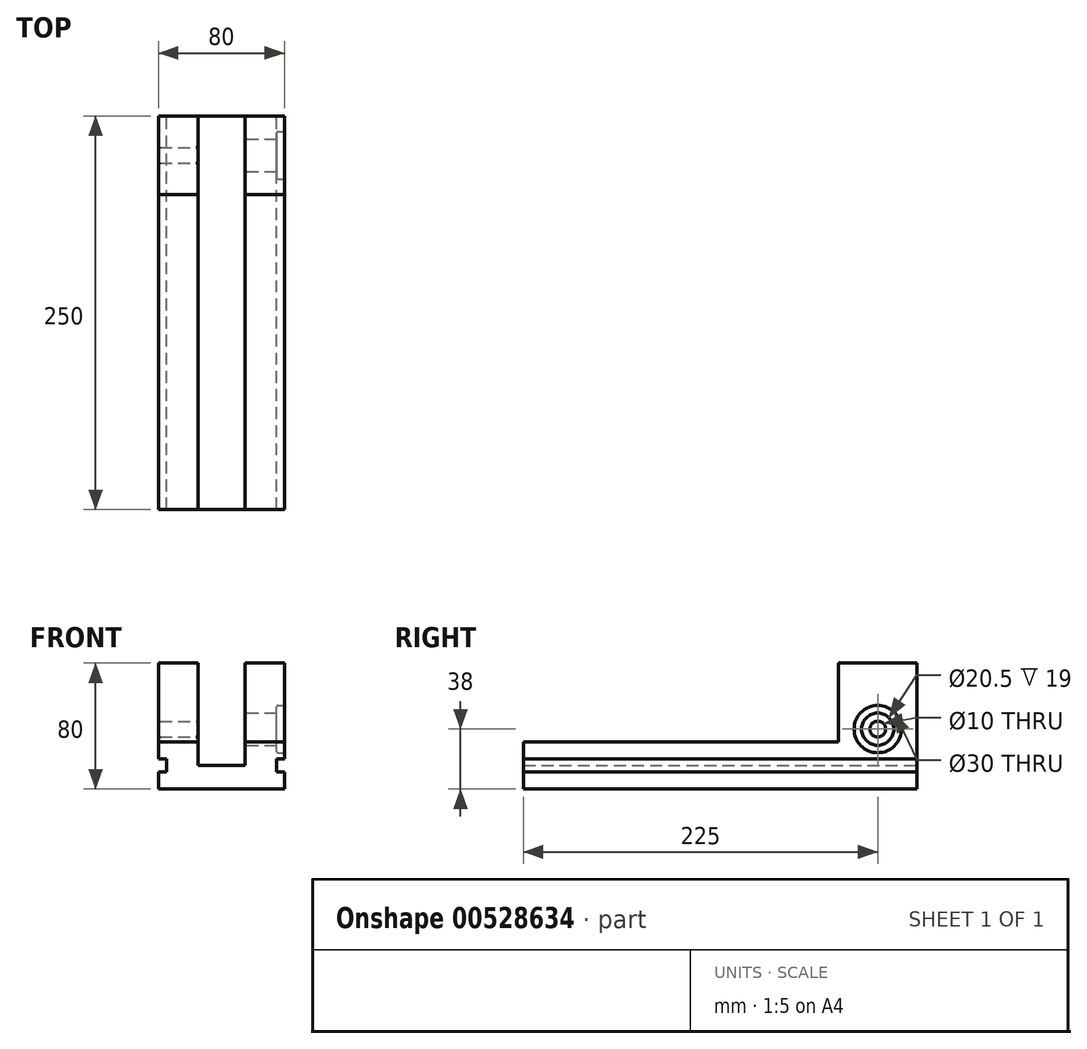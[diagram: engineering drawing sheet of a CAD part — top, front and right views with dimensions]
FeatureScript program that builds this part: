
annotation { "Feature Type Name" : "Feature", "Feature Type Description" : "" }
export const myFeature = defineFeature(function(context is Context, id is Id, definition is map)
    precondition{}
    {
        {
            var Q0;
            Q0=qCreatedBy(makeId("Front.planeOp"),FACE);
            var sketch = newSketch(context, id + "F0", { "sketchPlane" : qUnion([Q0])});
            skLineSegment(sketch, "E0.bottom", {"start": v(40, -15) * mm, "end": v(-40, -15) * mm});
            skLineSegment(sketch, "E0.top", {"start": v(40, 15) * mm, "end": v(15, 15) * mm});
            skLineSegment(sketch, "E0.left", {"start": v(40, -15) * mm, "end": v(40, -4) * mm});
            skLineSegment(sketch, "E0.right", {"start": v(-40, -15) * mm, "end": v(-40, -4) * mm});
            skPoint(sketch, "E0.middle", {"position": v(0, 0) * mm});
            skLineSegment(sketch, "E1", {"start": v(-15, 0) * mm, "end": v(15, 0) * mm});
            skLineSegment(sketch, "E2", {"start": v(-15, 0) * mm, "end": v(-15, 15) * mm});
            skLineSegment(sketch, "E3", {"start": v(15, 0) * mm, "end": v(15, 15) * mm});
            skLineSegment(sketch, "E4.trimOffspring", {"start": v(-15, 15) * mm, "end": v(-40, 15) * mm});
            skLineSegment(sketch, "E5", {"start": v(-40, 4) * mm, "end": v(-35, 4) * mm});
            skLineSegment(sketch, "E6", {"start": v(-35, 4) * mm, "end": v(-35, -4) * mm});
            skLineSegment(sketch, "E7", {"start": v(-35, -4) * mm, "end": v(-40, -4) * mm});
            skLineSegment(sketch, "E8.MirrorCS", {"start": v(35, 4) * mm, "end": v(35, -4) * mm});
            skLineSegment(sketch, "E9.MirrorCS", {"start": v(40, 4) * mm, "end": v(35, 4) * mm});
            skLineSegment(sketch, "E10.MirrorCS", {"start": v(35, -4) * mm, "end": v(40, -4) * mm});
            skLineSegment(sketch, "E11.trimOffspring", {"start": v(-40, 4) * mm, "end": v(-40, 15) * mm});
            skLineSegment(sketch, "E12.trimOffspring", {"start": v(40, 4) * mm, "end": v(40, 15) * mm});
            skSolve(sketch);
        }
        {
            var Q0;
            Q0=makeQuery(id+"F0.imprint","IMPRINT",FACE,{"disambiguationData":[TD([[makeQuery(id+"F0.imprint","IMPRINT",EDGE,{"derivedFrom":sQuery(id+"F0.wireOp",EDGE,"E0.bottom")}),-1.0]])]});
            extrude(context, id + "F1", {"entities" : qUnion([Q0]), "depth" : 250 * mm, "offsetDistance" : 25 * mm});
        }
        {
            var Q0;
            Q0=makeQuery(id+"F1.opExtrude","SWEPT_FACE",FACE,{"disambiguationData":[OSD([sQuery(id+"F0.wireOp",EDGE,"E4.trimOffspring")])]});
            var sketch = newSketch(context, id + "F2", { "sketchPlane" : qUnion([Q0])});
            skLineSegment(sketch, "E13.0.0", {"start": v(-15, 0) * mm, "end": v(-40, 0) * mm});
            skLineSegment(sketch, "E13.0.1", {"start": v(-40, 0) * mm, "end": v(-40, -250) * mm});
            skLineSegment(sketch, "E13.0.2", {"start": v(-40, -250) * mm, "end": v(-15, -250) * mm});
            skLineSegment(sketch, "E13.0.3", {"start": v(-15, -250) * mm, "end": v(-15, 0) * mm});
            skLineSegment(sketch, "E14.0.0", {"start": v(40, 0) * mm, "end": v(15, 0) * mm});
            skLineSegment(sketch, "E14.0.1", {"start": v(15, 0) * mm, "end": v(15, -250) * mm});
            skLineSegment(sketch, "E14.0.2", {"start": v(15, -250) * mm, "end": v(40, -250) * mm});
            skLineSegment(sketch, "E14.0.3", {"start": v(40, -250) * mm, "end": v(40, 0) * mm});
            skLineSegment(sketch, "E15", {"start": v(-40, -50) * mm, "end": v(-15, -50) * mm});
            skLineSegment(sketch, "E16.MirrorCS", {"start": v(40, -50) * mm, "end": v(15, -50) * mm});
            skSolve(sketch);
        }
        {
            var Q0;
            {var subQ0=sQuery(id+"F2.wireOp",EDGE,"E13.0.0");Q0=makeQuery(id+"F2.imprint","IMPRINT",FACE,{"disambiguationData":[TD([[makeQuery(id+"F2.imprint","IMPRINT",EDGE,{"derivedFrom":subQ0}),1.0]])]});}
            var Q1;
            {var subQ0=sQuery(id+"F2.wireOp",EDGE,"E14.0.0");Q1=makeQuery(id+"F2.imprint","IMPRINT",FACE,{"disambiguationData":[TD([[makeQuery(id+"F2.imprint","IMPRINT",EDGE,{"derivedFrom":subQ0}),1.0]])]});}
            extrude(context, id + "F3", {"entities" : qUnion([Q0, Q1]), "operationType" : NewBodyOperationType.ADD, "depth" : 50 * mm, "offsetDistance" : 25 * mm});
        }
        {
            var Q0;
            Q0=makeQuery(id+"F3.boolean.opBoolean","MERGE",FACE,{"derivedFrom":[makeQuery(id+"F1.opExtrude","SWEPT_FACE",FACE,{"disambiguationData":[OSD([sQuery(id+"F0.wireOp",EDGE,"E12.trimOffspring")])]}),makeQuery(id+"F3.opExtrude","SWEPT_FACE",FACE,{"disambiguationData":[OSD([sQuery(id+"F2.wireOp",EDGE,"E14.0.3")])]})]});
            var sketch = newSketch(context, id + "F4", { "sketchPlane" : qUnion([Q0])});
            skCircle(sketch, "E17", {"center": v(-25, 23) * mm, "radius": 5 * mm});
            skPoint(sketch, "E17.centerSnap0", {"position": v(-25, 65) * mm});
            skCircle(sketch, "E18", {"center": v(-25, 23) * mm, "radius": 10.25 * mm});
            skCircle(sketch, "E19", {"center": v(-25, 23) * mm, "radius": 15 * mm});
            skSolve(sketch);
        }
        {
            var Q0;
            Q0=makeQuery(id+"F4.imprint","IMPRINT",FACE,{"disambiguationData":[TD([[makeQuery(id+"F4.imprint","IMPRINT",EDGE,{"derivedFrom":sQuery(id+"F4.wireOp",EDGE,"E17")}),1.0]])]});
            extrude(context, id + "F5", {"entities" : qUnion([Q0]), "operationType" : NewBodyOperationType.REMOVE, "oppositeDirection" : true, "depth" : 100 * mm, "offsetDistance" : 25 * mm});
        }
        {
            var Q0;
            Q0=makeQuery(id+"F4.imprint","IMPRINT",FACE,{"disambiguationData":[TD([[makeQuery(id+"F4.imprint","IMPRINT",EDGE,{"derivedFrom":sQuery(id+"F4.wireOp",EDGE,"E17")}),-1.0]])]});
            extrude(context, id + "F6", {"entities" : qUnion([Q0]), "operationType" : NewBodyOperationType.REMOVE, "oppositeDirection" : true, "depth" : 25.8 * mm, "offsetDistance" : 25 * mm});
        }
        {
            var Q0;
            Q0=makeQuery(id+"F4.imprint","IMPRINT",FACE,{"disambiguationData":[TD([[makeQuery(id+"F4.imprint","IMPRINT",EDGE,{"derivedFrom":sQuery(id+"F4.wireOp",EDGE,"E18")}),-1.0]])]});
            extrude(context, id + "F7", {"entities" : qUnion([Q0]), "operationType" : NewBodyOperationType.REMOVE, "oppositeDirection" : true, "depth" : 5 * mm, "offsetDistance" : 25 * mm});
        }
        {
            var Q0;
            Q0=makeQuery(id+"F7.boolean.opBoolean","COPY",EDGE,{"derivedFrom":makeQuery(id+"F7.opExtrude","CAP_EDGE",EDGE,{"disambiguationData":[OSD([sQuery(id+"F4.wireOp",EDGE,"E19")])],"isStart":false})});
            var Q1;
            Q1=makeQuery(id+"F7.boolean.opBoolean","COPY",EDGE,{"derivedFrom":makeQuery(id+"F7.opExtrude","CAP_EDGE",EDGE,{"disambiguationData":[OSD([sQuery(id+"F4.wireOp",EDGE,"E18")])],"isStart":false})});
            var Q2;
            Q2=makeQuery(id+"F6.boolean.opBoolean","INTERSECT",EDGE,{"derivedFrom":[makeQuery(id+"F3.boolean.opBoolean","MERGE",FACE,{"derivedFrom":[makeQuery(id+"F1.opExtrude","SWEPT_FACE",FACE,{"disambiguationData":[OSD([sQuery(id+"F0.wireOp",EDGE,"E3")])]}),makeQuery(id+"F3.opExtrude","SWEPT_FACE",FACE,{"disambiguationData":[OSD([sQuery(id+"F2.wireOp",EDGE,"E14.0.1")])]})]}),makeQuery(id+"F6.opExtrude","SWEPT_FACE",FACE,{"disambiguationData":[OSD([sQuery(id+"F4.wireOp",EDGE,"E18")])]})]});
            var Q3;
            Q3=makeQuery(id+"F5.boolean.opBoolean","COPY",FACE,{"disambiguationData":[TD([makeQuery(id+"F1.opExtrude","SWEPT_FACE",FACE,{"disambiguationData":[OSD([sQuery(id+"F0.wireOp",EDGE,"E2")])]})])],"derivedFrom":makeQuery(id+"F5.opExtrude","SWEPT_FACE",FACE,{"disambiguationData":[OSD([sQuery(id+"F4.wireOp",EDGE,"E17")])]})});
            var Q4;
            Q4=makeQuery(id+"F7.boolean.opBoolean","COPY",EDGE,{"derivedFrom":makeQuery(id+"F7.opExtrude","CAP_EDGE",EDGE,{"disambiguationData":[OSD([sQuery(id+"F4.wireOp",EDGE,"E19")])],"isStart":true})});
            fillet(context, id + "F8", {"entities" : qUnion([Q0, Q1, Q2, Q3, Q4]), "radius" : 1 * mm, "tangentPropagation" : true, "allowEdgeOverflow" : false});
        }
    });
